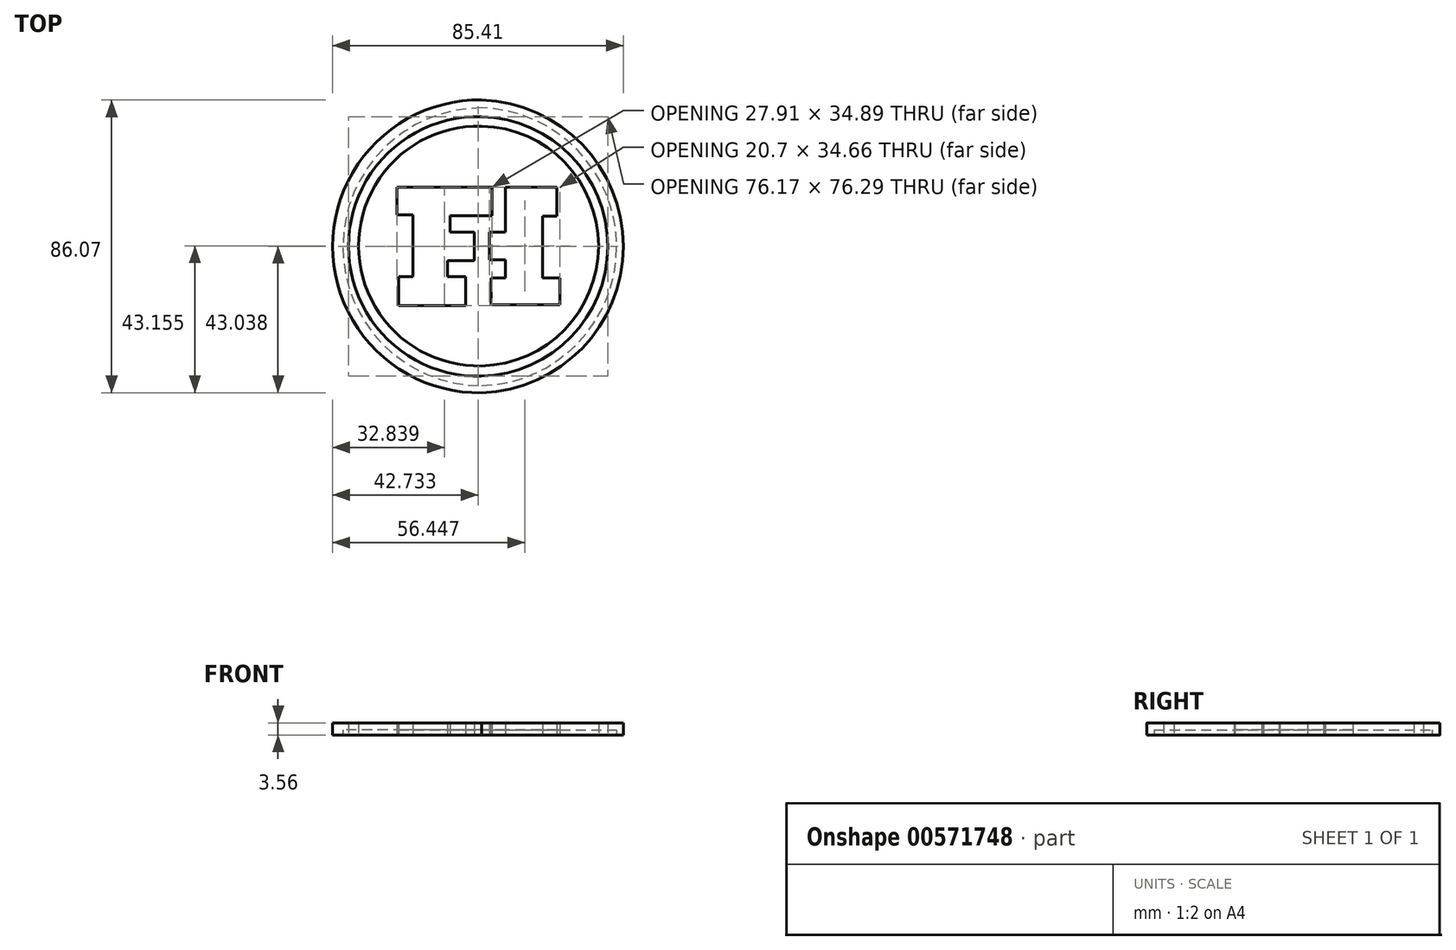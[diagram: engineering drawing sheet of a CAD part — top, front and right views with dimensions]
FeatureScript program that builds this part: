
annotation { "Feature Type Name" : "Feature", "Feature Type Description" : "" }
export const myFeature = defineFeature(function(context is Context, id is Id, definition is map)
    precondition{}
    {
        {
            var Q0;
            Q0=qCreatedBy(makeId("Top.planeOp"),FACE);
            var sketch = newSketch(context, id + "F0", { "sketchPlane" : qUnion([Q0])});
            skLineSegment(sketch, "E0", {"start": v(-24.93, 17.33) * mm, "end": v(-24.93, 8.72) * mm});
            skLineSegment(sketch, "E1", {"start": v(-24.93, 8.72) * mm, "end": v(-20.27, 8.72) * mm});
            skLineSegment(sketch, "E2", {"start": v(-20.27, 8.72) * mm, "end": v(-20.27, -9.42) * mm});
            skLineSegment(sketch, "E3", {"start": v(-20.27, -9.42) * mm, "end": v(-24.46, -9.42) * mm});
            skLineSegment(sketch, "E4", {"start": v(-24.46, -9.42) * mm, "end": v(-24.46, -18.03) * mm});
            skLineSegment(sketch, "E5", {"start": v(-24.46, -18.03) * mm, "end": v(-4.7, -18.03) * mm});
            skLineSegment(sketch, "E6", {"start": v(-4.7, -18.03) * mm, "end": v(-4.7, -9.42) * mm});
            skLineSegment(sketch, "E7", {"start": v(-4.7, -9.42) * mm, "end": v(-10.04, -9.42) * mm});
            skLineSegment(sketch, "E8", {"start": v(-10.04, -9.42) * mm, "end": v(-10.04, -4.77) * mm});
            skLineSegment(sketch, "E9", {"start": v(-10.04, -4.77) * mm, "end": v(-2.13, -4.77) * mm});
            skLineSegment(sketch, "E10", {"start": v(-2.13, -4.77) * mm, "end": v(-2.13, 3.6) * mm});
            skLineSegment(sketch, "E11", {"start": v(-2.13, 3.6) * mm, "end": v(-9.34, 3.6) * mm});
            skLineSegment(sketch, "E12", {"start": v(-9.34, 3.6) * mm, "end": v(-9.34, 8.49) * mm});
            skLineSegment(sketch, "E13", {"start": v(-9.34, 8.49) * mm, "end": v(2.98, 8.49) * mm});
            skLineSegment(sketch, "E14", {"start": v(2.98, 8.49) * mm, "end": v(2.98, 16.86) * mm});
            skLineSegment(sketch, "E15", {"start": v(2.98, 16.86) * mm, "end": v(-24.93, 16.86) * mm});
            skLineSegment(sketch, "E16", {"start": v(6.94, 16.86) * mm, "end": v(6.94, 3.6) * mm});
            skLineSegment(sketch, "E17", {"start": v(6.94, 3.6) * mm, "end": v(2.29, 3.6) * mm});
            skLineSegment(sketch, "E18", {"start": v(2.29, 3.6) * mm, "end": v(2.29, -4.54) * mm});
            skLineSegment(sketch, "E19", {"start": v(2.29, -4.54) * mm, "end": v(6.94, -4.54) * mm});
            skLineSegment(sketch, "E20", {"start": v(6.94, -4.54) * mm, "end": v(6.94, -9.88) * mm});
            skLineSegment(sketch, "E21", {"start": v(6.94, -9.88) * mm, "end": v(2.75, -9.88) * mm});
            skLineSegment(sketch, "E22", {"start": v(2.75, -9.88) * mm, "end": v(2.75, -17.8) * mm});
            skLineSegment(sketch, "E23", {"start": v(2.75, -17.8) * mm, "end": v(22.99, -17.8) * mm});
            skLineSegment(sketch, "E24", {"start": v(22.99, -17.8) * mm, "end": v(22.99, -9.88) * mm});
            skLineSegment(sketch, "E25", {"start": v(22.99, -9.88) * mm, "end": v(17.87, -9.88) * mm});
            skLineSegment(sketch, "E26", {"start": v(17.87, -9.88) * mm, "end": v(17.87, 8.26) * mm});
            skLineSegment(sketch, "E27", {"start": v(17.87, 8.26) * mm, "end": v(22.06, 8.26) * mm});
            skLineSegment(sketch, "E28", {"start": v(22.06, 8.26) * mm, "end": v(22.06, 16.86) * mm});
            skLineSegment(sketch, "E29", {"start": v(22.06, 16.86) * mm, "end": v(6.94, 16.86) * mm});
            skArc(sketch, "E30", {"start": v(0, 34.77) * mm, "mid": v(-36.17, -0.47) * mm, "end": v(0, -35.7) * mm});
            skArc(sketch, "E31", {"start": v(0, -35.7) * mm, "mid": v(34.33, -0.47) * mm, "end": v(0, 34.77) * mm});
            skArc(sketch, "E32", {"start": v(0, 42.45) * mm, "mid": v(-43.8, -0.58) * mm, "end": v(0, -43.61) * mm});
            skArc(sketch, "E33", {"start": v(0, -43.61) * mm, "mid": v(41.6, -0.58) * mm, "end": v(0, 42.45) * mm});
            skArc(sketch, "E34", {"start": v(0, 37.56) * mm, "mid": v(-39.16, -0.58) * mm, "end": v(0, -38.73) * mm});
            skArc(sketch, "E35", {"start": v(0, -38.73) * mm, "mid": v(37.01, -0.58) * mm, "end": v(0, 37.56) * mm});
            skSolve(sketch);
        }
        {
            var Q0;
            Q0 = qSketchRegion(id + "F0", true);
            extrude(context, id + "F1", {"entities" : qUnion([Q0]), "depth" : 3.56 * mm, "offsetDistance" : 25.4 * mm});
        }
        {
            var Q0;
            {var subQ1=sQuery(id+"F0.wireOp",EDGE,"E1");Q0=makeQuery(id+"F0.imprint","IMPRINT",FACE,{"disambiguationData":[TD([[makeQuery(id+"F0.imprint","IMPRINT",EDGE,{"derivedFrom":subQ1}),-1.0]])]});}
            extrude(context, id + "F2", {"entities" : qUnion([Q0]), "depth" : 3.56 * mm, "offsetDistance" : 25.4 * mm});
        }
        {
            var Q0;
            {var subQ0=sQuery(id+"F0.wireOp",EDGE,"E1");Q0=makeQuery(id+"F0.imprint","IMPRINT",FACE,{"disambiguationData":[TD([[makeQuery(id+"F0.imprint","IMPRINT",EDGE,{"derivedFrom":subQ0}),1.0]])]});}
            var Q1;
            Q1=makeQuery(id+"F0.imprint","IMPRINT",FACE,{"disambiguationData":[TD([[makeQuery(id+"F0.imprint","IMPRINT",EDGE,{"derivedFrom":sQuery(id+"F0.wireOp",EDGE,"E16")}),1.0]])]});
            extrude(context, id + "F3", {"entities" : qUnion([Q0, Q1]), "depth" : 1.52 * mm, "offsetDistance" : 25.4 * mm});
        }
        {
            var Q0;
            Q0=qCreatedBy(makeId("Top.planeOp"),FACE);
            var sketch = newSketch(context, id + "F4", { "sketchPlane" : qUnion([Q0])});
            skArc(sketch, "E36", {"start": v(0, 40.12) * mm, "mid": v(-40.79, -0.7) * mm, "end": v(0, -41.52) * mm});
            skArc(sketch, "E37", {"start": v(0, -41.52) * mm, "mid": v(39.65, -0.7) * mm, "end": v(0, 40.12) * mm});
            skSolve(sketch);
        }
        {
            var Q0;
            Q0 = qSketchRegion(id + "F4", true);
            extrude(context, id + "F5", {"entities" : qUnion([Q0]), "depth" : 1.52 * mm, "offsetDistance" : 25.4 * mm});
        }
    });
